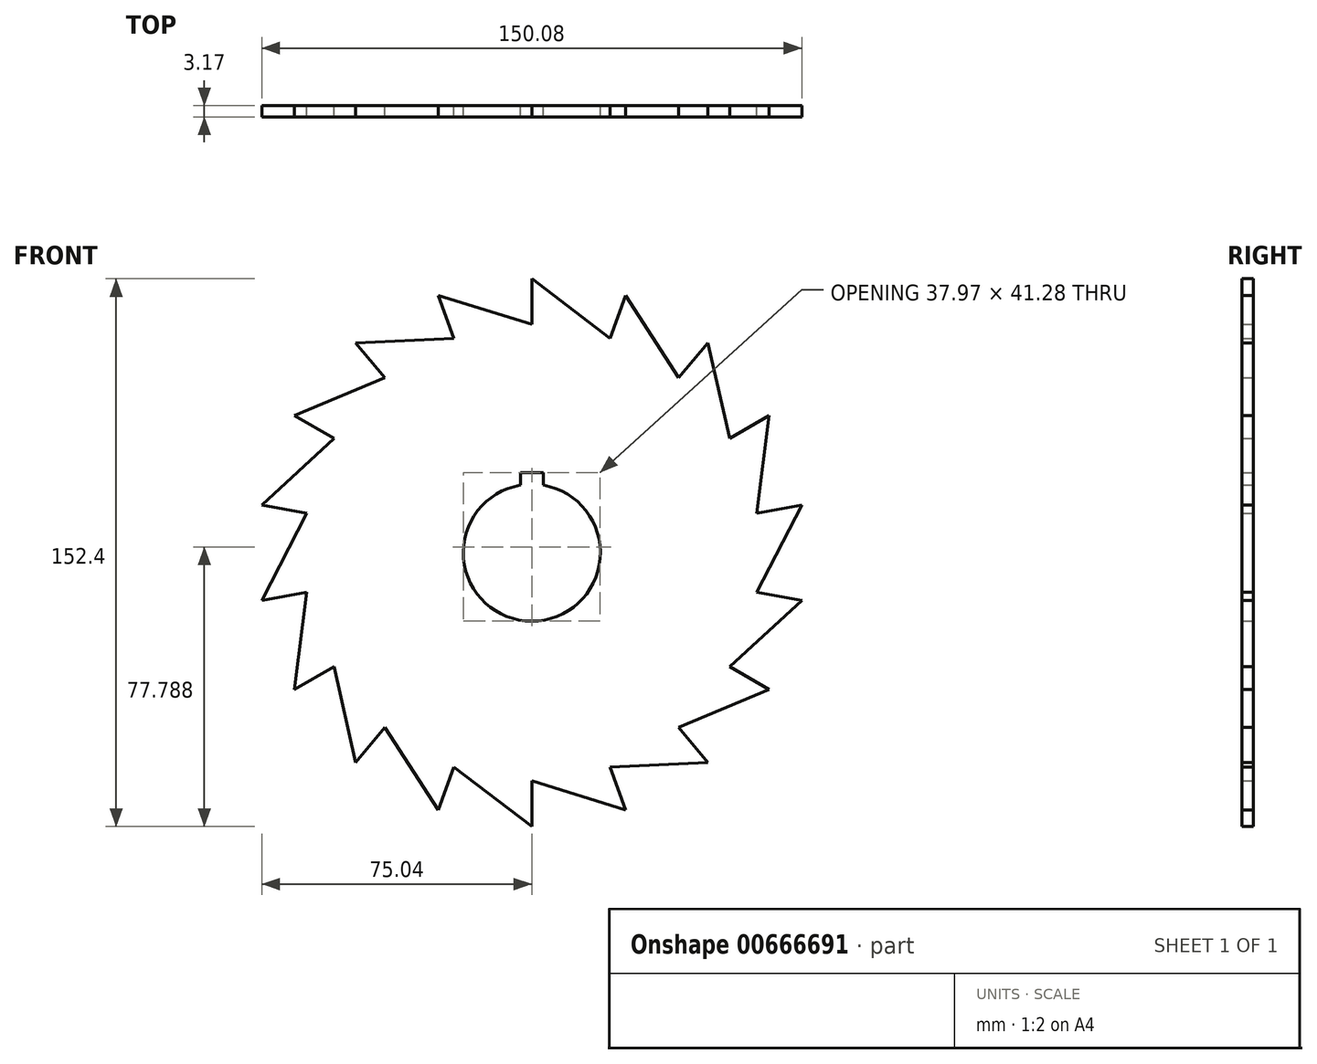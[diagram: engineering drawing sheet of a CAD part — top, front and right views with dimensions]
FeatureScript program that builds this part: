
annotation { "Feature Type Name" : "Feature", "Feature Type Description" : "" }
export const myFeature = defineFeature(function(context is Context, id is Id, definition is map)
    precondition{}
    {
        {
            var Q0;
            Q0=qCreatedBy(makeId("Front.planeOp"),FACE);
            var sketch = newSketch(context, id + "F0", { "sketchPlane" : qUnion([Q0])});
            skCircle(sketch, "E0", {"center": v(0, 0) * mm, "radius": 63.5 * mm});
            skCircle(sketch, "E1", {"center": v(0, 0) * mm, "radius": 76.2 * mm, "construction": true});
            skLineSegment(sketch, "E2", {"start": v(0, 63.5) * mm, "end": v(0, 76.2) * mm});
            skLineSegment(sketch, "E3", {"start": v(0, 76.2) * mm, "end": v(21.72, 59.67) * mm});
            skCircle(sketch, "E4", {"center": v(0, 0) * mm, "radius": 19.05 * mm});
            skLineSegment(sketch, "E5", {"start": v(0, 22.23) * mm, "end": v(3.18, 22.23) * mm});
            skLineSegment(sketch, "E6", {"start": v(3.17, 22.23) * mm, "end": v(3.18, 18.78) * mm});
            skLineSegment(sketch, "E7.MirrorCS", {"start": v(0, 22.23) * mm, "end": v(-3.18, 22.23) * mm});
            skLineSegment(sketch, "E8.MirrorCS", {"start": v(-3.18, 22.23) * mm, "end": v(-3.18, 18.78) * mm});
            skLineSegment(sketch, "E9", {"start": v(0, 63.5) * mm, "end": v(0, 0) * mm, "construction": true});
            skLineSegment(sketch, "E10", {"start": v(21.72, 59.67) * mm, "end": v(0, 0) * mm, "construction": true});
            skLineSegment(sketch, "E11.1.0", {"start": v(-21.72, 59.67) * mm, "end": v(-26.06, 71.6) * mm});
            skLineSegment(sketch, "E11.1.1", {"start": v(-26.06, 71.6) * mm, "end": v(0, 63.5) * mm});
            skLineSegment(sketch, "E11.2.0", {"start": v(-40.82, 48.64) * mm, "end": v(-48.98, 58.37) * mm});
            skLineSegment(sketch, "E11.2.1", {"start": v(-48.98, 58.37) * mm, "end": v(-21.72, 59.67) * mm});
            skLineSegment(sketch, "E12.1.3.0", {"start": v(-55, 31.75) * mm, "end": v(-66, 38.1) * mm});
            skLineSegment(sketch, "E12.3.3.0", {"start": v(-66, 38.1) * mm, "end": v(-40.82, 48.64) * mm});
            skLineSegment(sketch, "E12.1.4.0", {"start": v(-62.54, 11.03) * mm, "end": v(-75.04, 13.23) * mm});
            skLineSegment(sketch, "E12.3.4.0", {"start": v(-75.04, 13.23) * mm, "end": v(-55, 31.75) * mm});
            skLineSegment(sketch, "E12.1.5.0", {"start": v(-62.54, -11.03) * mm, "end": v(-75.04, -13.23) * mm});
            skLineSegment(sketch, "E12.3.5.0", {"start": v(-75.04, -13.23) * mm, "end": v(-62.54, 11.03) * mm});
            skLineSegment(sketch, "E12.1.6.0", {"start": v(-55, -31.75) * mm, "end": v(-66, -38.1) * mm});
            skLineSegment(sketch, "E12.3.6.0", {"start": v(-66, -38.1) * mm, "end": v(-62.54, -11.03) * mm});
            skLineSegment(sketch, "E12.1.7.0", {"start": v(-40.82, -48.64) * mm, "end": v(-48.98, -58.37) * mm});
            skLineSegment(sketch, "E12.3.7.0", {"start": v(-48.98, -58.37) * mm, "end": v(-55, -31.75) * mm});
            skLineSegment(sketch, "E12.1.8.0", {"start": v(-21.72, -59.67) * mm, "end": v(-26.06, -71.6) * mm});
            skLineSegment(sketch, "E12.3.8.0", {"start": v(-26.06, -71.6) * mm, "end": v(-40.82, -48.64) * mm});
            skLineSegment(sketch, "E12.1.9.0", {"start": v(0, -63.5) * mm, "end": v(0, -76.2) * mm});
            skLineSegment(sketch, "E12.3.9.0", {"start": v(0, -76.2) * mm, "end": v(-21.72, -59.67) * mm});
            skLineSegment(sketch, "E12.1.10.0", {"start": v(21.72, -59.67) * mm, "end": v(26.06, -71.6) * mm});
            skLineSegment(sketch, "E12.3.10.0", {"start": v(26.06, -71.6) * mm, "end": v(0, -63.5) * mm});
            skLineSegment(sketch, "E12.1.11.0", {"start": v(40.82, -48.64) * mm, "end": v(48.98, -58.37) * mm});
            skLineSegment(sketch, "E12.3.11.0", {"start": v(48.98, -58.37) * mm, "end": v(21.72, -59.67) * mm});
            skLineSegment(sketch, "E12.1.12.0", {"start": v(55, -31.75) * mm, "end": v(66, -38.1) * mm});
            skLineSegment(sketch, "E12.3.12.0", {"start": v(66, -38.1) * mm, "end": v(40.82, -48.64) * mm});
            skLineSegment(sketch, "E12.1.13.0", {"start": v(62.54, -11.03) * mm, "end": v(75.04, -13.23) * mm});
            skLineSegment(sketch, "E12.3.13.0", {"start": v(75.04, -13.23) * mm, "end": v(55, -31.75) * mm});
            skLineSegment(sketch, "E12.1.14.0", {"start": v(62.54, 11.03) * mm, "end": v(75.04, 13.23) * mm});
            skLineSegment(sketch, "E12.3.14.0", {"start": v(75.04, 13.23) * mm, "end": v(62.54, -11.03) * mm});
            skLineSegment(sketch, "E12.1.15.0", {"start": v(55, 31.75) * mm, "end": v(66, 38.1) * mm});
            skLineSegment(sketch, "E12.3.15.0", {"start": v(66, 38.1) * mm, "end": v(62.54, 11.03) * mm});
            skLineSegment(sketch, "E12.1.16.0", {"start": v(40.82, 48.64) * mm, "end": v(48.98, 58.37) * mm});
            skLineSegment(sketch, "E12.3.16.0", {"start": v(48.98, 58.37) * mm, "end": v(55, 31.75) * mm});
            skLineSegment(sketch, "E12.1.17.0", {"start": v(21.72, 59.67) * mm, "end": v(26.06, 71.6) * mm});
            skLineSegment(sketch, "E12.3.17.0", {"start": v(26.06, 71.6) * mm, "end": v(40.82, 48.64) * mm});
            skSolve(sketch);
        }
        {
            var Q0;
            {var subQ2=sQuery(id+"F0.wireOp",EDGE,"E12.1.5.0");Q0=makeQuery(id+"F0.imprint","IMPRINT",FACE,{"disambiguationData":[TD([[makeQuery(id+"F0.imprint","IMPRINT",EDGE,{"derivedFrom":subQ2}),-1.0]])]});}
            var Q1;
            {var subQ2=sQuery(id+"F0.wireOp",EDGE,"E12.1.4.0");Q1=makeQuery(id+"F0.imprint","IMPRINT",FACE,{"disambiguationData":[TD([[makeQuery(id+"F0.imprint","IMPRINT",EDGE,{"derivedFrom":subQ2}),-1.0]])]});}
            var Q2;
            {var subQ2=sQuery(id+"F0.wireOp",EDGE,"E12.1.3.0");Q2=makeQuery(id+"F0.imprint","IMPRINT",FACE,{"disambiguationData":[TD([[makeQuery(id+"F0.imprint","IMPRINT",EDGE,{"derivedFrom":subQ2}),-1.0]])]});}
            var Q3;
            {var subQ2=sQuery(id+"F0.wireOp",EDGE,"E11.2.0");Q3=makeQuery(id+"F0.imprint","IMPRINT",FACE,{"disambiguationData":[TD([[makeQuery(id+"F0.imprint","IMPRINT",EDGE,{"derivedFrom":subQ2}),-1.0]])]});}
            var Q4;
            {var subQ2=sQuery(id+"F0.wireOp",EDGE,"E12.1.6.0");Q4=makeQuery(id+"F0.imprint","IMPRINT",FACE,{"disambiguationData":[TD([[makeQuery(id+"F0.imprint","IMPRINT",EDGE,{"derivedFrom":subQ2}),-1.0]])]});}
            var Q5;
            {var subQ2=sQuery(id+"F0.wireOp",EDGE,"E12.1.7.0");Q5=makeQuery(id+"F0.imprint","IMPRINT",FACE,{"disambiguationData":[TD([[makeQuery(id+"F0.imprint","IMPRINT",EDGE,{"derivedFrom":subQ2}),-1.0]])]});}
            var Q6;
            {var subQ2=sQuery(id+"F0.wireOp",EDGE,"E12.1.8.0");Q6=makeQuery(id+"F0.imprint","IMPRINT",FACE,{"disambiguationData":[TD([[makeQuery(id+"F0.imprint","IMPRINT",EDGE,{"derivedFrom":subQ2}),-1.0]])]});}
            var Q7;
            {var subQ2=sQuery(id+"F0.wireOp",EDGE,"E12.1.9.0");Q7=makeQuery(id+"F0.imprint","IMPRINT",FACE,{"disambiguationData":[TD([[makeQuery(id+"F0.imprint","IMPRINT",EDGE,{"derivedFrom":subQ2}),-1.0]])]});}
            var Q8;
            {var subQ2=sQuery(id+"F0.wireOp",EDGE,"E12.1.10.0");Q8=makeQuery(id+"F0.imprint","IMPRINT",FACE,{"disambiguationData":[TD([[makeQuery(id+"F0.imprint","IMPRINT",EDGE,{"derivedFrom":subQ2}),-1.0]])]});}
            var Q9;
            {var subQ2=sQuery(id+"F0.wireOp",EDGE,"E12.1.11.0");Q9=makeQuery(id+"F0.imprint","IMPRINT",FACE,{"disambiguationData":[TD([[makeQuery(id+"F0.imprint","IMPRINT",EDGE,{"derivedFrom":subQ2}),-1.0]])]});}
            var Q10;
            {var subQ2=sQuery(id+"F0.wireOp",EDGE,"E12.1.12.0");Q10=makeQuery(id+"F0.imprint","IMPRINT",FACE,{"disambiguationData":[TD([[makeQuery(id+"F0.imprint","IMPRINT",EDGE,{"derivedFrom":subQ2}),-1.0]])]});}
            var Q11;
            {var subQ2=sQuery(id+"F0.wireOp",EDGE,"E12.1.13.0");Q11=makeQuery(id+"F0.imprint","IMPRINT",FACE,{"disambiguationData":[TD([[makeQuery(id+"F0.imprint","IMPRINT",EDGE,{"derivedFrom":subQ2}),-1.0]])]});}
            var Q12;
            {var subQ2=sQuery(id+"F0.wireOp",EDGE,"E12.1.14.0");Q12=makeQuery(id+"F0.imprint","IMPRINT",FACE,{"disambiguationData":[TD([[makeQuery(id+"F0.imprint","IMPRINT",EDGE,{"derivedFrom":subQ2}),-1.0]])]});}
            var Q13;
            {var subQ2=sQuery(id+"F0.wireOp",EDGE,"E12.1.15.0");Q13=makeQuery(id+"F0.imprint","IMPRINT",FACE,{"disambiguationData":[TD([[makeQuery(id+"F0.imprint","IMPRINT",EDGE,{"derivedFrom":subQ2}),-1.0]])]});}
            var Q14;
            {var subQ2=sQuery(id+"F0.wireOp",EDGE,"E12.1.16.0");Q14=makeQuery(id+"F0.imprint","IMPRINT",FACE,{"disambiguationData":[TD([[makeQuery(id+"F0.imprint","IMPRINT",EDGE,{"derivedFrom":subQ2}),-1.0]])]});}
            var Q15;
            {var subQ0=sQuery(id+"F0.wireOp",EDGE,"E12.1.17.0");Q15=makeQuery(id+"F0.imprint","IMPRINT",FACE,{"disambiguationData":[TD([[makeQuery(id+"F0.imprint","IMPRINT",EDGE,{"derivedFrom":subQ0}),-1.0]])]});}
            var Q16;
            {var subQ0=sQuery(id+"F0.wireOp",EDGE,"E2");Q16=makeQuery(id+"F0.imprint","IMPRINT",FACE,{"disambiguationData":[TD([[makeQuery(id+"F0.imprint","IMPRINT",EDGE,{"derivedFrom":subQ0}),-1.0]])]});}
            var Q17;
            {var subQ2=sQuery(id+"F0.wireOp",EDGE,"E11.1.0");Q17=makeQuery(id+"F0.imprint","IMPRINT",FACE,{"disambiguationData":[TD([[makeQuery(id+"F0.imprint","IMPRINT",EDGE,{"derivedFrom":subQ2}),-1.0]])]});}
            var Q18;
            Q18=makeQuery(id+"F0.imprint","IMPRINT",FACE,{"disambiguationData":[TD([[makeQuery(id+"F0.imprint","IMPRINT",EDGE,{"derivedFrom":sQuery(id+"F0.wireOp",EDGE,"E5")}),1.0]])]});
            extrude(context, id + "F1", {"entities" : qUnion([Q0, Q1, Q2, Q3, Q4, Q5, Q6, Q7, Q8, Q9, Q10, Q11, Q12, Q13, Q14, Q15, Q16, Q17, Q18]), "depth" : 3.17 * mm, "offsetDistance" : 25.4 * mm});
        }
    });
